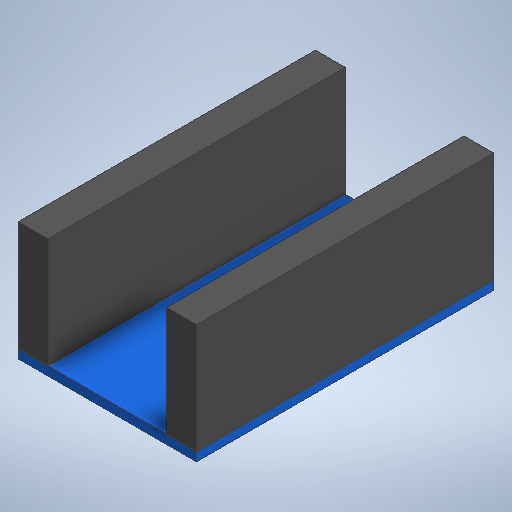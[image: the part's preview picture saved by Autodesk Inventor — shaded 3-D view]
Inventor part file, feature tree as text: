
AUTODESK INVENTOR PART (.ipt)
format: ipt  version: 2025 (Build 290162000, 162)  size: 208,384 bytes
history: native  units: in
note: dims shown in document units (in); Inventor stores cm internally (conversion verified against a paired STEP export)
features: extrude x2, sketch x2, projected_geometry x1
ambient origin geometry x8: Origin, YZ Plane, XZ Plane, XY Plane, X Axis, Y Axis, Z Axis, Center Point
bodies: Solid1 (feature_tree), Solid2 (feature_tree)
feature tree (5):
  extrude  "Extrusion1"  Depth=1.0in
  extrude  "Extrusion3"  Depth=0.1in
  sketch  "Sketch1"  dims[d0=0.6in d1=1.0in]
  sketch  "Sketch3"  dims[d2=0.03in d3=0.0in d7=0.1in d8=0.1in d9=0.37in d10=0.0in]
  projected_geometry  "Projected Loop2"
